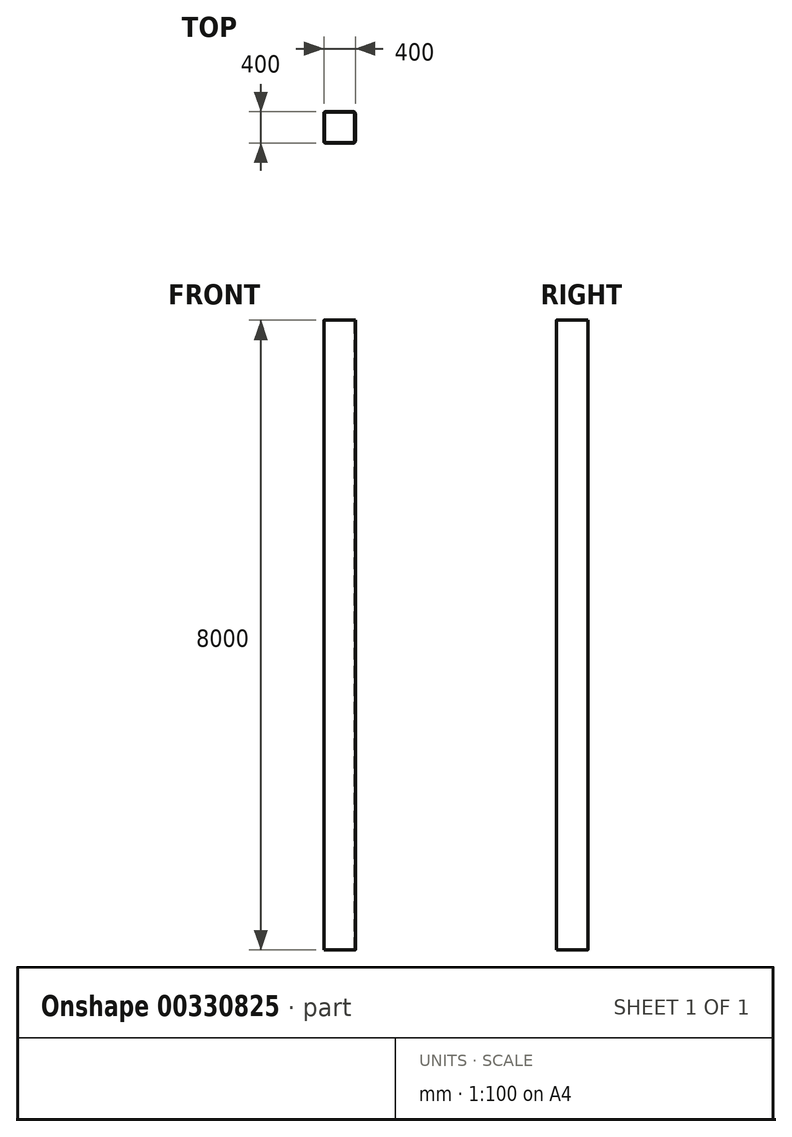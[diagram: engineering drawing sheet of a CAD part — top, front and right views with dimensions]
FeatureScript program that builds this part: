
annotation { "Feature Type Name" : "Feature", "Feature Type Description" : "" }
export const myFeature = defineFeature(function(context is Context, id is Id, definition is map)
    precondition{}
    {
        {
            var Q0;
            Q0=qCreatedBy(makeId("Top.planeOp"),FACE);
            var sketch = newSketch(context, id + "F0", { "sketchPlane" : qUnion([Q0])});
            skLineSegment(sketch, "E0.bottom", {"start": v(175, -200) * mm, "end": v(-175, -200) * mm});
            skLineSegment(sketch, "E0.top", {"start": v(175, 200) * mm, "end": v(-175, 200) * mm});
            skLineSegment(sketch, "E0.left", {"start": v(200, -175) * mm, "end": v(200, 175) * mm});
            skLineSegment(sketch, "E0.right", {"start": v(-200, -175) * mm, "end": v(-200, 175) * mm});
            skPoint(sketch, "E0.middle", {"position": v(0, 0) * mm});
            skPoint(sketch, "E1.visualSharp", {"position": v(200, -200) * mm});
            skArc(sketch, "E1.filletArc", {"start": v(175, -200) * mm, "mid": v(192.68, -192.68) * mm, "end": v(200, -175) * mm});
            skPoint(sketch, "E2.visualSharp", {"position": v(200, 200) * mm});
            skArc(sketch, "E2.filletArc", {"start": v(200, 175) * mm, "mid": v(192.68, 192.68) * mm, "end": v(175, 200) * mm});
            skPoint(sketch, "E3.visualSharp", {"position": v(-200, 200) * mm});
            skArc(sketch, "E3.filletArc", {"start": v(-175, 200) * mm, "mid": v(-192.68, 192.68) * mm, "end": v(-200, 175) * mm});
            skPoint(sketch, "E4.visualSharp", {"position": v(-200, -200) * mm});
            skArc(sketch, "E4.filletArc", {"start": v(-200, -175) * mm, "mid": v(-192.68, -192.68) * mm, "end": v(-175, -200) * mm});
            skSolve(sketch);
        }
        {
            var Q0;
            Q0=makeQuery(id+"F0.imprint","IMPRINT",FACE,{"disambiguationData":[TD([[makeQuery(id+"F0.imprint","IMPRINT",EDGE,{"derivedFrom":sQuery(id+"F0.wireOp",EDGE,"E0.bottom")}),-1.0]])]});
            extrude(context, id + "F1", {"entities" : qUnion([Q0]), "depth" : 8000 * mm});
        }
        {
            var Q0;
            Q0=makeQuery(id+"F1.opExtrude","CAP_FACE",FACE,{"disambiguationData":[OSD([sQuery(id+"F0.wireOp",EDGE,"E0.bottom"),sQuery(id+"F0.wireOp",EDGE,"E0.top"),sQuery(id+"F0.wireOp",EDGE,"E0.left"),sQuery(id+"F0.wireOp",EDGE,"E0.right"),sQuery(id+"F0.wireOp",EDGE,"E1.filletArc"),sQuery(id+"F0.wireOp",EDGE,"E2.filletArc"),sQuery(id+"F0.wireOp",EDGE,"E3.filletArc"),sQuery(id+"F0.wireOp",EDGE,"E4.filletArc")])],"isStart":false});
            shell(context, id + "F2", {"entities" : qUnion([Q0]), "thickness" : 8 * mm});
        }
    });
